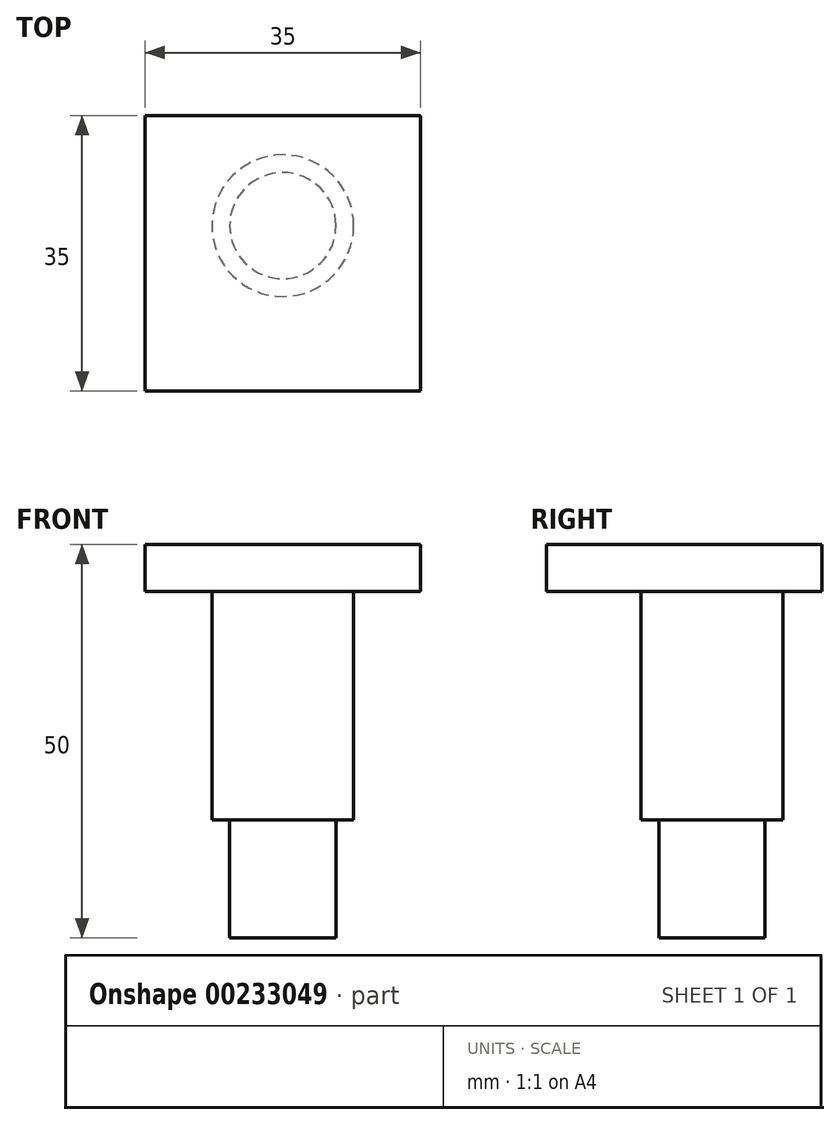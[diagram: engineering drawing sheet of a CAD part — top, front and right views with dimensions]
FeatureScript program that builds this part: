
annotation { "Feature Type Name" : "Feature", "Feature Type Description" : "" }
export const myFeature = defineFeature(function(context is Context, id is Id, definition is map)
    precondition{}
    {
        {
            var Q0;
            Q0=qCreatedBy(makeId("Top.planeOp"),FACE);
            cPlane(context, id + "F0", {"entities" : qUnion([Q0]), "cplaneType" : CPlaneType.OFFSET, "offset" : 40 * mm, "width" : 150 * mm, "height" : 150 * mm});
        }
        {
            var Q0;
            Q0=qCreatedBy(id+"F0.planeOp",FACE);
            var sketch = newSketch(context, id + "F1", { "sketchPlane" : qUnion([Q0])});
            skCircle(sketch, "E0", {"center": v(0, 0) * mm, "radius": 6.75 * mm});
            skSolve(sketch);
        }
        {
            var Q0;
            Q0=makeQuery(id+"F1.imprint","IMPRINT",FACE,{"disambiguationData":[TD([[makeQuery(id+"F1.imprint","IMPRINT",EDGE,{"derivedFrom":sQuery(id+"F1.wireOp",EDGE,"E0")}),1.0]])]});
            extrude(context, id + "F2", {"entities" : qUnion([Q0]), "oppositeDirection" : true, "depth" : 15 * mm});
        }
        {
            var Q0;
            Q0=qCreatedBy(id+"F0.planeOp",FACE);
            var sketch = newSketch(context, id + "F3", { "sketchPlane" : qUnion([Q0])});
            skCircle(sketch, "E1", {"center": v(0, 0) * mm, "radius": 9 * mm});
            skSolve(sketch);
        }
        {
            var Q0;
            Q0=makeQuery(id+"F3.imprint","IMPRINT",FACE,{"disambiguationData":[TD([[makeQuery(id+"F3.imprint","IMPRINT",EDGE,{"derivedFrom":sQuery(id+"F3.wireOp",EDGE,"E1")}),1.0]])]});
            extrude(context, id + "F4", {"entities" : qUnion([Q0]), "operationType" : NewBodyOperationType.ADD, "depth" : 35 * mm, "offsetDistance" : 25 * mm});
        }
        {
            var Q0;
            Q0=makeQuery(id+"F4.opExtrude","CAP_FACE",FACE,{"disambiguationData":[OSD([sQuery(id+"F3.wireOp",EDGE,"E1")])],"isStart":false});
            var sketch = newSketch(context, id + "F5", { "sketchPlane" : qUnion([Q0])});
            skLineSegment(sketch, "E2.bottom", {"start": v(-17.5, 14) * mm, "end": v(17.5, 14) * mm});
            skLineSegment(sketch, "E2.top", {"start": v(-17.5, -21) * mm, "end": v(17.5, -21) * mm});
            skLineSegment(sketch, "E2.left", {"start": v(-17.5, 14) * mm, "end": v(-17.5, -21) * mm});
            skLineSegment(sketch, "E2.right", {"start": v(17.5, 14) * mm, "end": v(17.5, -21) * mm});
            skSolve(sketch);
        }
        {
            var Q0;
            Q0=makeQuery(id+"F5.imprint","IMPRINT",FACE,{"disambiguationData":[TD([[makeQuery(id+"F5.imprint","IMPRINT",EDGE,{"derivedFrom":sQuery(id+"F5.wireOp",EDGE,"E2.bottom")}),-1.0]])]});
            extrude(context, id + "F6", {"entities" : qUnion([Q0]), "operationType" : NewBodyOperationType.ADD, "oppositeDirection" : true, "depth" : 6 * mm});
        }
    });
